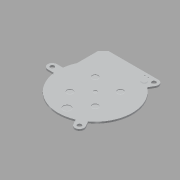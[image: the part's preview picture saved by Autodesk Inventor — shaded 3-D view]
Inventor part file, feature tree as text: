
AUTODESK INVENTOR PART (.ipt)
format: ipt  version: 2020 (Build 240168000, 168)  size: 194,560 bytes
history: native  units: mm
features: extrude x3, sketch x2, projected_geometry x1
ambient origin geometry x8: Origin, YZ Plane, XZ Plane, XY Plane, X Axis, Y Axis, Z Axis, Center Point
bodies: Solid1 (feature_tree)
feature tree (6):
  extrude  "Extrusion1"  Depth=42.5mm
  extrude  "Extrusion2"  Depth=1.6mm TaperAngle=0.0deg
  extrude  "Extrusion3"  Depth=0.5mm TaperAngle=0.0deg
  sketch  "Sketch2"  dims[d1=4.0mm d2=42.5mm]
  projected_geometry  "Projected Loop1"
  sketch  "Sketch3"  dims[d3=30.0mm d5=360.0deg d19=1.6mm d20=0.0mm d22=40.0mm d23=35.0mm d24=360.0deg d25=12.5mm d26=12.5mm d27=6.0mm d28=360.0deg d29=0.5mm d30=0.0mm d31=3.35mm d32=28.0mm d33=7.5mm d34=11.0mm d36=38.1mm d37=3.4mm d38=0.762mm d39=2.7mm d40=2.5mm d41=0.762mm d42=2.54mm d43=6.85mm d44=1.502mm d45=1.0mm d46=0.0mm]
